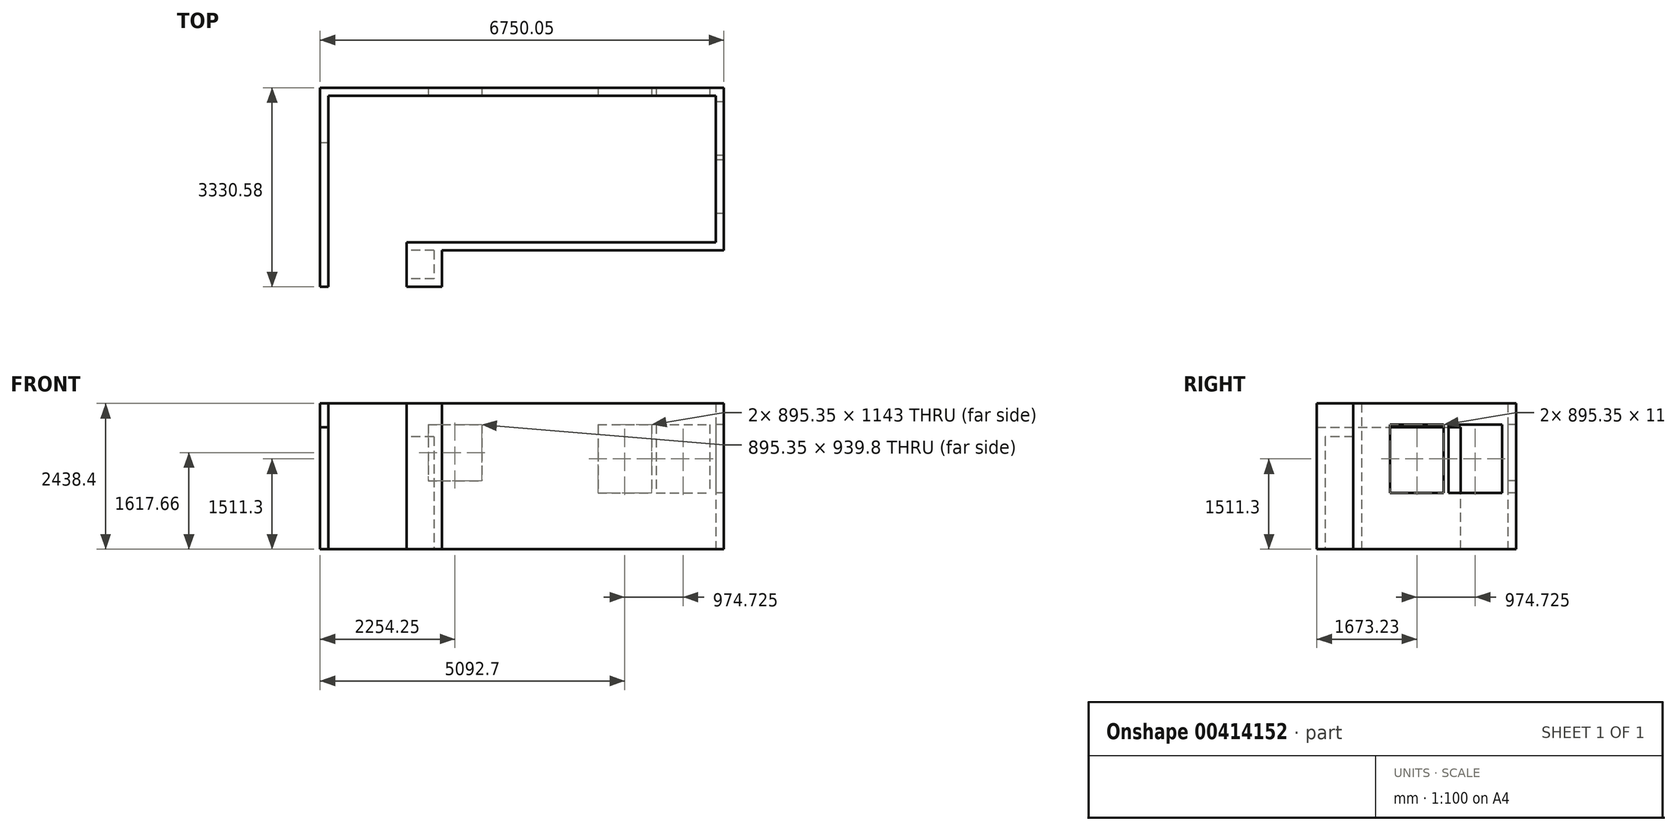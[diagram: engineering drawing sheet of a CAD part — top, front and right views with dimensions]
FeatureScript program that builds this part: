
annotation { "Feature Type Name" : "Feature", "Feature Type Description" : "" }
export const myFeature = defineFeature(function(context is Context, id is Id, definition is map)
    precondition{}
    {
        {
            var Q0;
            Q0=qCreatedBy(makeId("Top.planeOp"),FACE);
            var sketch = newSketch(context, id + "F0", { "sketchPlane" : qUnion([Q0])});
            skLineSegment(sketch, "E0", {"start": v(-2415.82, 1870.8) * mm, "end": v(4061.18, 1870.8) * mm});
            skLineSegment(sketch, "E1", {"start": v(4061.18, 1870.8) * mm, "end": v(4061.18, -577.13) * mm});
            skLineSegment(sketch, "E2", {"start": v(4061.18, -577.13) * mm, "end": v(-1106.2, -577.13) * mm});
            skLineSegment(sketch, "E3", {"start": v(-2415.82, 1870.8) * mm, "end": v(-2415.82, -1323.26) * mm});
            skLineSegment(sketch, "E4", {"start": v(-2415.82, -1323.26) * mm, "end": v(-2552.35, -1323.26) * mm});
            skLineSegment(sketch, "E5", {"start": v(-2552.35, -1323.26) * mm, "end": v(-2552.35, 2007.32) * mm});
            skLineSegment(sketch, "E6", {"start": v(-2552.35, 2007.32) * mm, "end": v(4197.7, 2007.32) * mm});
            skLineSegment(sketch, "E7", {"start": v(4197.7, 2007.32) * mm, "end": v(4197.7, -713.66) * mm});
            skLineSegment(sketch, "E8", {"start": v(4197.7, -713.66) * mm, "end": v(-512.47, -713.66) * mm});
            skLineSegment(sketch, "E9", {"start": v(-512.47, -1323.26) * mm, "end": v(-1106.2, -1323.26) * mm});
            skLineSegment(sketch, "E10", {"start": v(-512.47, -1323.26) * mm, "end": v(-512.47, -713.66) * mm});
            skLineSegment(sketch, "E11", {"start": v(-649, -713.66) * mm, "end": v(-649, -1186.73) * mm});
            skLineSegment(sketch, "E12", {"start": v(-649, -1186.73) * mm, "end": v(-1106.2, -1186.73) * mm});
            skLineSegment(sketch, "E13", {"start": v(-1106.2, -1186.73) * mm, "end": v(-1106.2, -1323.26) * mm});
            skLineSegment(sketch, "E14", {"start": v(-649, -713.66) * mm, "end": v(-1106.2, -713.66) * mm});
            skLineSegment(sketch, "E15", {"start": v(-1106.2, -713.66) * mm, "end": v(-1106.2, -577.13) * mm});
            skSolve(sketch);
        }
        {
            var Q0;
            Q0 = qSketchRegion(id + "F0", true);
            extrude(context, id + "F1", {"entities" : qUnion([Q0]), "depth" : 2438.4 * mm});
        }
        {
            var Q0;
            Q0=makeQuery(id+"F1.opExtrude","SWEPT_FACE",FACE,{"disambiguationData":[OSD([sQuery(id+"F0.wireOp",EDGE,"E0")])]});
            var sketch = newSketch(context, id + "F2", { "sketchPlane" : qUnion([Q0])});
            skLineSegment(sketch, "E16.bottom", {"start": v(-745.77, 2087.56) * mm, "end": v(149.58, 2087.56) * mm});
            skLineSegment(sketch, "E16.top", {"start": v(-745.77, 1147.76) * mm, "end": v(149.58, 1147.76) * mm});
            skLineSegment(sketch, "E16.left", {"start": v(-745.77, 2087.56) * mm, "end": v(-745.77, 1147.76) * mm});
            skLineSegment(sketch, "E16.right", {"start": v(149.58, 2087.56) * mm, "end": v(149.58, 1147.76) * mm});
            skLineSegment(sketch, "E17.bottom", {"start": v(2092.68, 2082.8) * mm, "end": v(2988.03, 2082.8) * mm});
            skLineSegment(sketch, "E17.top", {"start": v(2092.68, 939.8) * mm, "end": v(2988.03, 939.8) * mm});
            skLineSegment(sketch, "E17.left", {"start": v(2092.68, 2082.8) * mm, "end": v(2092.68, 939.8) * mm});
            skLineSegment(sketch, "E17.right", {"start": v(2988.03, 2082.8) * mm, "end": v(2988.03, 939.8) * mm});
            skLineSegment(sketch, "E18.bottom", {"start": v(3067.4, 2082.8) * mm, "end": v(3962.75, 2082.8) * mm});
            skLineSegment(sketch, "E18.top", {"start": v(3067.4, 939.8) * mm, "end": v(3962.75, 939.8) * mm});
            skLineSegment(sketch, "E18.left", {"start": v(3067.4, 2082.8) * mm, "end": v(3067.4, 939.8) * mm});
            skLineSegment(sketch, "E18.right", {"start": v(3962.75, 2082.8) * mm, "end": v(3962.75, 939.8) * mm});
            skSolve(sketch);
        }
        {
            var Q0;
            Q0 = qSketchRegion(id + "F2", true);
            extrude(context, id + "F3", {"entities" : qUnion([Q0]), "operationType" : NewBodyOperationType.REMOVE, "endBound" : BoundingType.UP_TO_NEXT, "oppositeDirection" : true, "depth" : 25.4 * mm});
        }
        {
            var Q0;
            Q0=makeQuery(id+"F1.opExtrude","SWEPT_FACE",FACE,{"disambiguationData":[OSD([sQuery(id+"F0.wireOp",EDGE,"E1")])]});
            var sketch = newSketch(context, id + "F4", { "sketchPlane" : qUnion([Q0])});
            skLineSegment(sketch, "E19.bottom", {"start": v(-1772.37, 2082.8) * mm, "end": v(-877.02, 2082.8) * mm});
            skLineSegment(sketch, "E19.top", {"start": v(-1772.37, 939.8) * mm, "end": v(-877.02, 939.8) * mm});
            skLineSegment(sketch, "E19.left", {"start": v(-1772.37, 2082.8) * mm, "end": v(-1772.37, 939.8) * mm});
            skLineSegment(sketch, "E19.right", {"start": v(-877.02, 2082.8) * mm, "end": v(-877.02, 939.8) * mm});
            skLineSegment(sketch, "E20.bottom", {"start": v(-797.64, 2082.8) * mm, "end": v(97.7, 2082.8) * mm});
            skLineSegment(sketch, "E20.top", {"start": v(-797.64, 939.8) * mm, "end": v(97.7, 939.8) * mm});
            skLineSegment(sketch, "E20.left", {"start": v(-797.64, 2082.8) * mm, "end": v(-797.64, 939.8) * mm});
            skLineSegment(sketch, "E20.right", {"start": v(97.7, 2082.8) * mm, "end": v(97.7, 939.8) * mm});
            skSolve(sketch);
        }
        {
            var Q0;
            Q0 = qSketchRegion(id + "F4", true);
            extrude(context, id + "F5", {"entities" : qUnion([Q0]), "operationType" : NewBodyOperationType.REMOVE, "endBound" : BoundingType.UP_TO_NEXT, "oppositeDirection" : true, "depth" : 25.4 * mm});
        }
        {
            var Q0;
            Q0=makeQuery(id+"F1.opExtrude","SWEPT_FACE",FACE,{"disambiguationData":[OSD([sQuery(id+"F0.wireOp",EDGE,"E5")])]});
            var sketch = newSketch(context, id + "F6", { "sketchPlane" : qUnion([Q0])});
            skLineSegment(sketch, "E21.bottom", {"start": v(1323.26, 0) * mm, "end": v(-1083.4, 0) * mm});
            skLineSegment(sketch, "E21.top", {"start": v(1323.26, 2041.53) * mm, "end": v(-1083.4, 2041.53) * mm});
            skLineSegment(sketch, "E21.left", {"start": v(1323.26, 0) * mm, "end": v(1323.26, 2041.53) * mm});
            skLineSegment(sketch, "E21.right", {"start": v(-1083.4, 0) * mm, "end": v(-1083.4, 2041.53) * mm});
            skSolve(sketch);
        }
        {
            var Q0;
            Q0 = qSketchRegion(id + "F6", true);
            extrude(context, id + "F7", {"entities" : qUnion([Q0]), "operationType" : NewBodyOperationType.REMOVE, "endBound" : BoundingType.UP_TO_NEXT, "oppositeDirection" : true, "depth" : 25.4 * mm});
        }
        {
            var Q0;
            Q0=makeQuery(id+"F1.opExtrude","CAP_FACE",FACE,{"disambiguationData":[OSD([sQuery(id+"F0.wireOp",EDGE,"E0"),sQuery(id+"F0.wireOp",EDGE,"E1"),sQuery(id+"F0.wireOp",EDGE,"E2"),sQuery(id+"F0.wireOp",EDGE,"E3"),sQuery(id+"F0.wireOp",EDGE,"E4"),sQuery(id+"F0.wireOp",EDGE,"E5"),sQuery(id+"F0.wireOp",EDGE,"E6"),sQuery(id+"F0.wireOp",EDGE,"E7"),sQuery(id+"F0.wireOp",EDGE,"E8"),sQuery(id+"F0.wireOp",EDGE,"E9"),sQuery(id+"F0.wireOp",EDGE,"E10"),sQuery(id+"F0.wireOp",EDGE,"E11"),sQuery(id+"F0.wireOp",EDGE,"E12"),sQuery(id+"F0.wireOp",EDGE,"E13"),sQuery(id+"F0.wireOp",EDGE,"E14"),sQuery(id+"F0.wireOp",EDGE,"E15")])],"isStart":false});
            var sketch = newSketch(context, id + "F8", { "sketchPlane" : qUnion([Q0])});
            skLineSegment(sketch, "E22.bottom", {"start": v(-649, -1186.73) * mm, "end": v(-1106.2, -1186.73) * mm});
            skLineSegment(sketch, "E22.top", {"start": v(-649, -713.66) * mm, "end": v(-1106.2, -713.66) * mm});
            skLineSegment(sketch, "E22.left", {"start": v(-649, -1186.73) * mm, "end": v(-649, -713.66) * mm});
            skLineSegment(sketch, "E22.right", {"start": v(-1106.2, -1186.73) * mm, "end": v(-1106.2, -713.66) * mm});
            skSolve(sketch);
        }
        {
            var Q0;
            Q0 = qSketchRegion(id + "F8", true);
            extrude(context, id + "F9", {"entities" : qUnion([Q0]), "operationType" : NewBodyOperationType.ADD, "oppositeDirection" : true, "depth" : 558.8 * mm});
        }
    });
